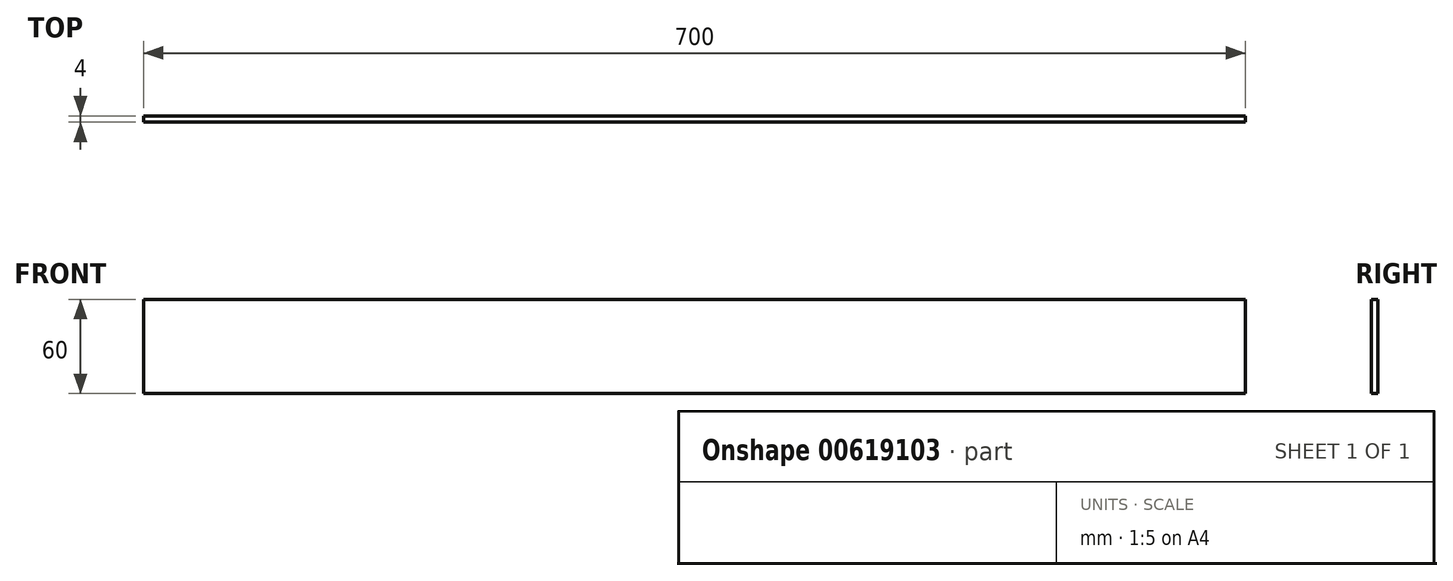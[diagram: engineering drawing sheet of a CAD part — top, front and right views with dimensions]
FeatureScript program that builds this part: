
annotation { "Feature Type Name" : "Feature", "Feature Type Description" : "" }
export const myFeature = defineFeature(function(context is Context, id is Id, definition is map)
    precondition{}
    {
        {
            var Q0;
            Q0=qCreatedBy(makeId("Front.planeOp"),FACE);
            var sketch = newSketch(context, id + "F0", { "sketchPlane" : qUnion([Q0])});
            skLineSegment(sketch, "E0.bottom", {"start": v(629.47, 0) * mm, "end": v(-70.53, 0) * mm});
            skLineSegment(sketch, "E0.top", {"start": v(629.47, 60) * mm, "end": v(-70.53, 60) * mm});
            skLineSegment(sketch, "E0.left", {"start": v(629.47, 0) * mm, "end": v(629.47, 60) * mm});
            skLineSegment(sketch, "E0.right", {"start": v(-70.53, 0) * mm, "end": v(-70.53, 60) * mm});
            skSolve(sketch);
        }
        {
            var Q0;
            Q0 = qSketchRegion(id + "F0", true);
            extrude(context, id + "F1", {"entities" : qUnion([Q0]), "depth" : 4 * mm, "offsetDistance" : 25 * mm});
        }
    });
